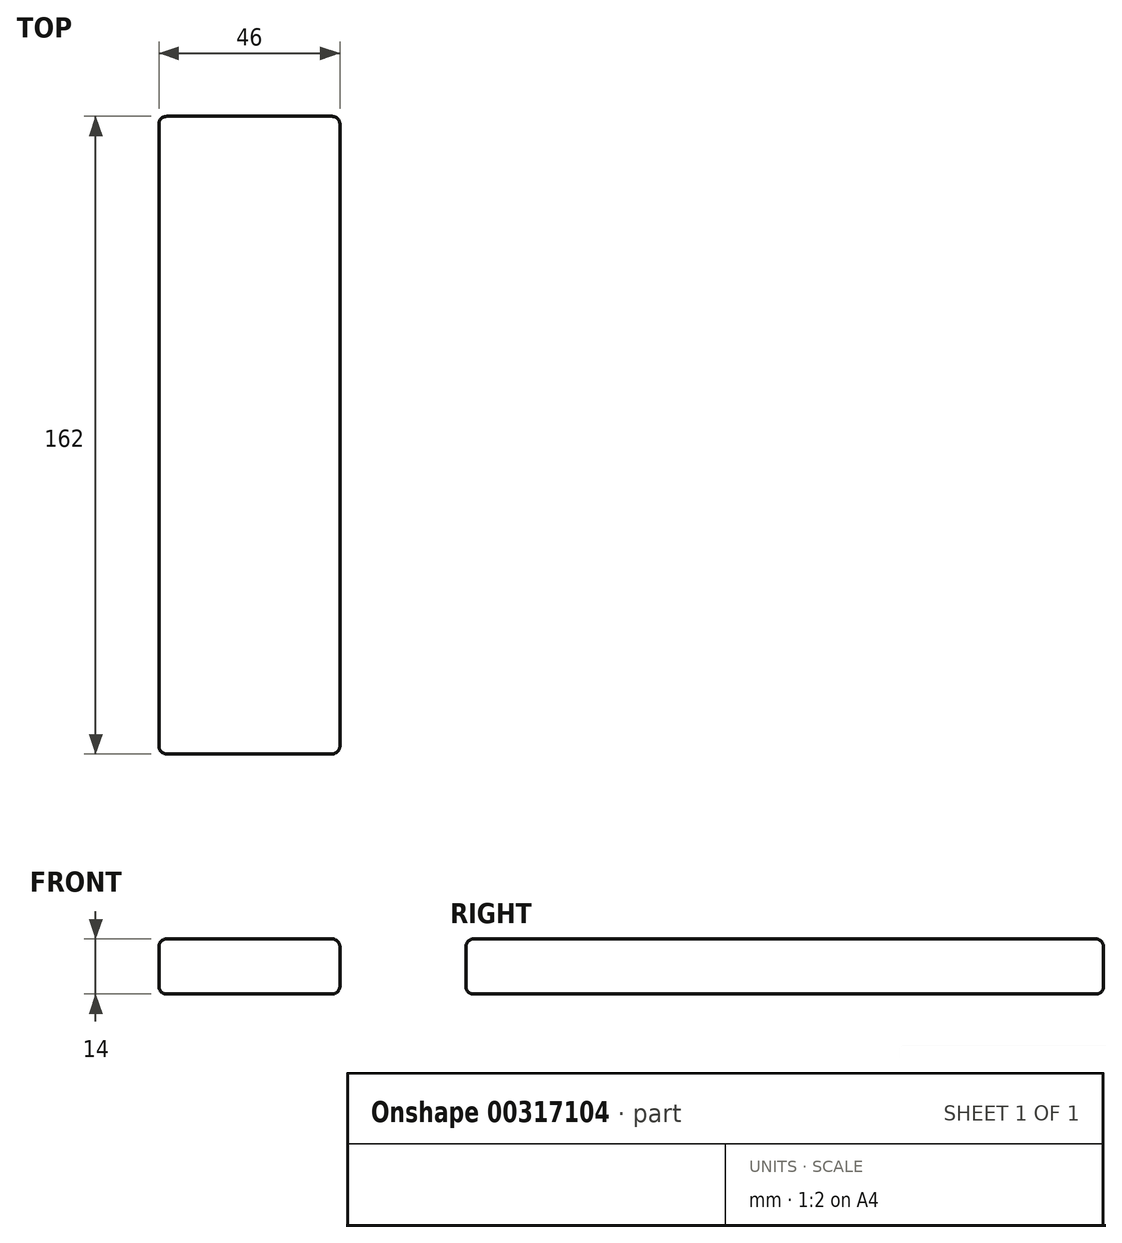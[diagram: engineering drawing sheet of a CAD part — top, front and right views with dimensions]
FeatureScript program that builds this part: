
annotation { "Feature Type Name" : "Feature", "Feature Type Description" : "" }
export const myFeature = defineFeature(function(context is Context, id is Id, definition is map)
    precondition{}
    {
        {
            var Q0;
            Q0=qCreatedBy(makeId("Top.planeOp"),FACE);
            var sketch = newSketch(context, id + "F0", { "sketchPlane" : qUnion([Q0])});
            skLineSegment(sketch, "E0.bottom", {"start": v(23, -81) * mm, "end": v(-23, -81) * mm});
            skLineSegment(sketch, "E0.top", {"start": v(23, 81) * mm, "end": v(-23, 81) * mm});
            skLineSegment(sketch, "E0.left", {"start": v(23, -81) * mm, "end": v(23, 81) * mm});
            skLineSegment(sketch, "E0.right", {"start": v(-23, -81) * mm, "end": v(-23, 81) * mm});
            skPoint(sketch, "E0.middle", {"position": v(0, 0) * mm});
            skSolve(sketch);
        }
        {
            var Q0;
            Q0 = qSketchRegion(id + "F0", true);
            extrude(context, id + "F1", {"entities" : qUnion([Q0]), "depth" : 14 * mm});
        }
        {
            var Q0;
            Q0=makeQuery(id+"F1.opExtrude","CAP_FACE",FACE,{"disambiguationData":[OSD([sQuery(id+"F0.wireOp",EDGE,"E0.bottom"),sQuery(id+"F0.wireOp",EDGE,"E0.top"),sQuery(id+"F0.wireOp",EDGE,"E0.left"),sQuery(id+"F0.wireOp",EDGE,"E0.right")])],"isStart":false});
            var Q1;
            Q1=makeQuery(id+"F1.opExtrude","CAP_FACE",FACE,{"disambiguationData":[OSD([sQuery(id+"F0.wireOp",EDGE,"E0.bottom"),sQuery(id+"F0.wireOp",EDGE,"E0.top"),sQuery(id+"F0.wireOp",EDGE,"E0.left"),sQuery(id+"F0.wireOp",EDGE,"E0.right")])],"isStart":true});
            var Q2;
            Q2=makeQuery(id+"F1.opExtrude","SWEPT_FACE",FACE,{"disambiguationData":[OSD([sQuery(id+"F0.wireOp",EDGE,"E0.left")])]});
            var Q3;
            Q3=makeQuery(id+"F1.opExtrude","SWEPT_FACE",FACE,{"disambiguationData":[OSD([sQuery(id+"F0.wireOp",EDGE,"E0.right")])]});
            fillet(context, id + "F2", {"entities" : qUnion([Q0, Q1, Q2, Q3]), "radius" : 2 * mm, "tangentPropagation" : true, "allowEdgeOverflow" : false});
        }
    });
